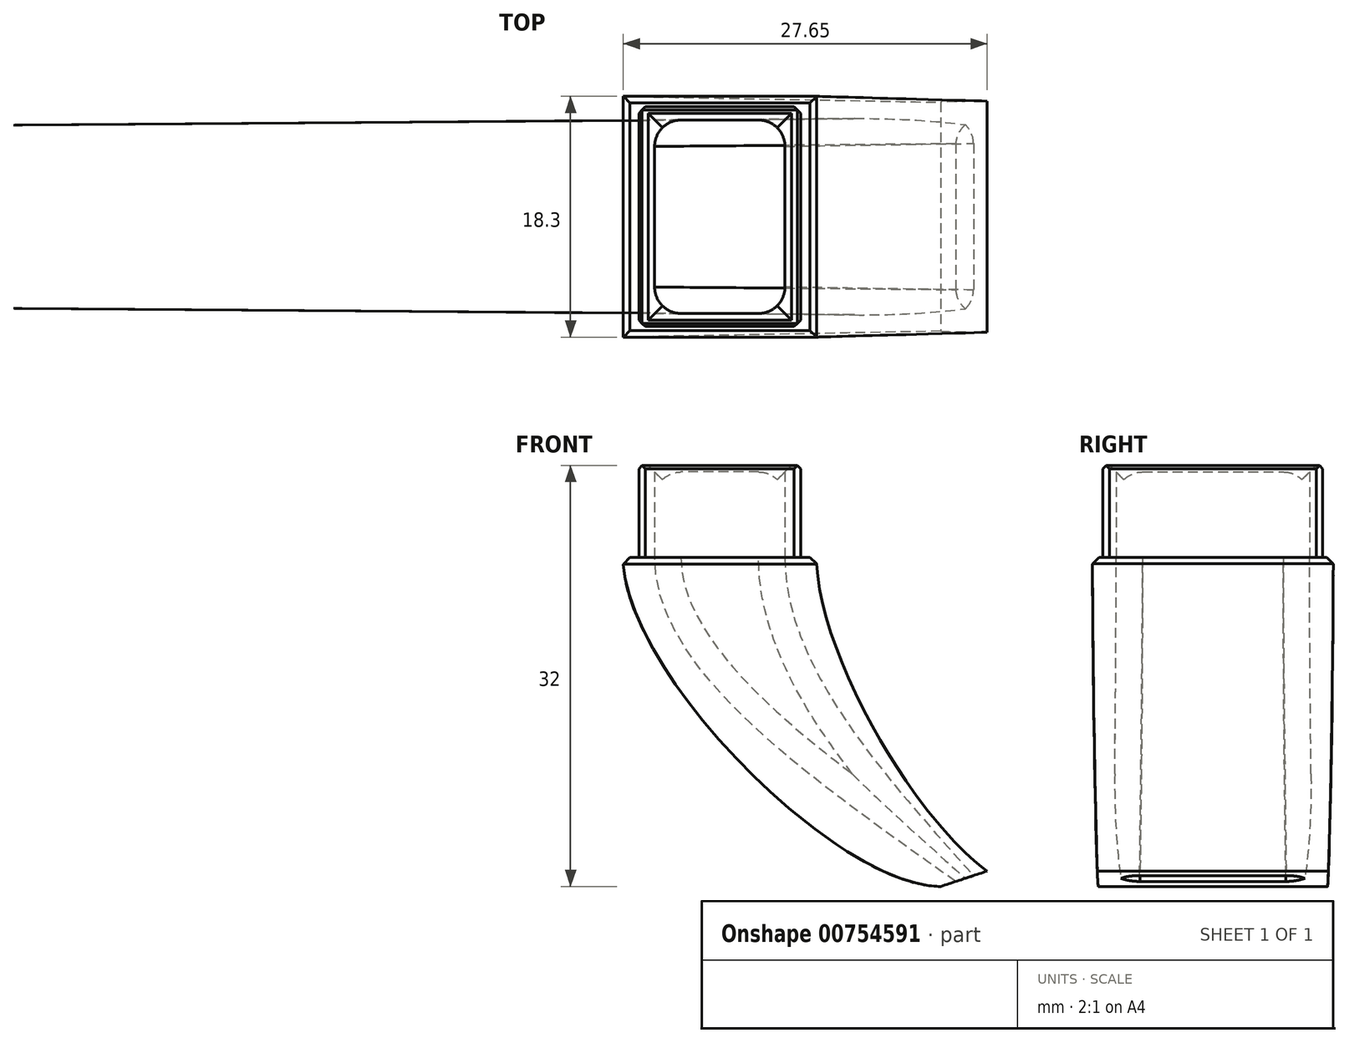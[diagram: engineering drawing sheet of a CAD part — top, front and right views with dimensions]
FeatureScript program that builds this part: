
annotation { "Feature Type Name" : "Feature", "Feature Type Description" : "" }
export const myFeature = defineFeature(function(context is Context, id is Id, definition is map)
    precondition{}
    {
        {
            var Q0;
            Q0=qCreatedBy(makeId("Top.planeOp"),FACE);
            var sketch = newSketch(context, id + "F0", { "sketchPlane" : qUnion([Q0])});
            skLineSegment(sketch, "E0.bottom", {"start": v(4.95, 7.35) * mm, "end": v(-4.95, 7.35) * mm});
            skLineSegment(sketch, "E0.top", {"start": v(4.95, -7.35) * mm, "end": v(-4.95, -7.35) * mm});
            skLineSegment(sketch, "E0.left", {"start": v(4.95, 7.35) * mm, "end": v(4.95, -7.35) * mm});
            skLineSegment(sketch, "E0.right", {"start": v(-4.95, 7.35) * mm, "end": v(-4.95, -7.35) * mm});
            skPoint(sketch, "E0.middle", {"position": v(0, 0) * mm});
            skLineSegment(sketch, "E1.bottom", {"start": v(6.15, 8.35) * mm, "end": v(-6.15, 8.35) * mm});
            skLineSegment(sketch, "E1.top", {"start": v(6.15, -8.35) * mm, "end": v(-6.15, -8.35) * mm});
            skLineSegment(sketch, "E1.left", {"start": v(6.15, 8.35) * mm, "end": v(6.15, -8.35) * mm});
            skLineSegment(sketch, "E1.right", {"start": v(-6.15, 8.35) * mm, "end": v(-6.15, -8.35) * mm});
            skSolve(sketch);
        }
        {
            var Q0;
            Q0 = qSketchRegion(id + "F0", true);
            extrude(context, id + "F1", {"entities" : qUnion([Q0]), "depth" : 7 * mm, "offsetDistance" : 25 * mm});
        }
        {
            var Q0;
            Q0=qCreatedBy(makeId("Top.planeOp"),FACE);
            var sketch = newSketch(context, id + "F2", { "sketchPlane" : qUnion([Q0])});
            skLineSegment(sketch, "E2.bottom", {"start": v(7.35, 9.15) * mm, "end": v(-7.35, 9.15) * mm});
            skLineSegment(sketch, "E2.top", {"start": v(7.35, -9.15) * mm, "end": v(-7.35, -9.15) * mm});
            skLineSegment(sketch, "E2.left", {"start": v(7.35, 9.15) * mm, "end": v(7.35, -9.15) * mm});
            skLineSegment(sketch, "E2.right", {"start": v(-7.35, 9.15) * mm, "end": v(-7.35, -9.15) * mm});
            skPoint(sketch, "E2.middle", {"position": v(0, 0) * mm});
            skSolve(sketch);
        }
        {
            var Q0;
            Q0=qCreatedBy(makeId("Top.planeOp"),FACE);
            cPlane(context, id + "F3", {"entities" : qUnion([Q0]), "cplaneType" : CPlaneType.OFFSET, "offset" : 25 * mm, "oppositeDirection" : true, "width" : 150 * mm, "height" : 150 * mm});
        }
        {
            var Q0;
            Q0=qCreatedBy(id+"F3.planeOp",FACE);
            var sketch = newSketch(context, id + "F4", { "sketchPlane" : qUnion([Q0])});
            skPoint(sketch, "E3.middle", {"position": v(20, 0) * mm});
            skLineSegment(sketch, "E4.bottom", {"start": v(23.2, 8.7) * mm, "end": v(16.8, 8.7) * mm});
            skLineSegment(sketch, "E4.top", {"start": v(23.2, -8.7) * mm, "end": v(16.8, -8.7) * mm});
            skLineSegment(sketch, "E4.left", {"start": v(23.2, 8.7) * mm, "end": v(23.2, -8.7) * mm});
            skLineSegment(sketch, "E4.right", {"start": v(16.8, 8.7) * mm, "end": v(16.8, -8.7) * mm});
            skSolve(sketch);
        }
        {
            var Q1;
            Q1 = qSketchRegion(id + "F2", true);
            var Q2;
            Q2 = qSketchRegion(id + "F4", true);
            loft(context, id + "F5", {"operationType" : NewBodyOperationType.ADD, "startCondition" : LoftEndDerivativeType.NORMAL_TO_PROFILE, "startMagnitude" : 1, "endCondition" : LoftEndDerivativeType.TANGENT_TO_PROFILE, "endMagnitude" : 1, "sheetProfilesArray" : [{ "sheetProfileEntities" : qUnion([Q1]) }, { "sheetProfileEntities" : qUnion([Q2]) }]});
        }
        {
            var Q0;
            Q0=qCreatedBy(makeId("Front.planeOp"),FACE);
            var sketch = newSketch(context, id + "F6", { "sketchPlane" : qUnion([Q0])});
            skLineSegment(sketch, "E5", {"start": v(16.8, -25) * mm, "end": v(20.4, -23.8) * mm});
            skLineSegment(sketch, "E6", {"start": v(20.4, -23.8) * mm, "end": v(25.23, -23.8) * mm});
            skLineSegment(sketch, "E7", {"start": v(25.23, -23.8) * mm, "end": v(25.23, -25) * mm});
            skLineSegment(sketch, "E8", {"start": v(25.23, -25) * mm, "end": v(16.8, -25) * mm});
            skSolve(sketch);
        }
        {
            var Q0;
            Q0 = qSketchRegion(id + "F6", true);
            extrude(context, id + "F7", {"entities" : qUnion([Q0]), "operationType" : NewBodyOperationType.REMOVE, "endBound" : BoundingType.SYMMETRIC, "oppositeDirection" : true, "depth" : 25 * mm, "offsetDistance" : 25 * mm});
        }
        {
            var Q0;
            Q0=makeQuery(id+"F7.boolean.opBoolean","COPY",FACE,{"derivedFrom":makeQuery(id+"F7.opExtrude","SWEPT_FACE",FACE,{"disambiguationData":[OSD([sQuery(id+"F6.wireOp",EDGE,"E5")])]})});
            var sketch = newSketch(context, id + "F8", { "sketchPlane" : qUnion([Q0])});
            skLineSegment(sketch, "E9.bottom", {"start": v(9.23, -7.56) * mm, "end": v(10.65, -7.56) * mm});
            skLineSegment(sketch, "E9.top", {"start": v(9.23, 7.56) * mm, "end": v(10.65, 7.56) * mm});
            skLineSegment(sketch, "E9.left", {"start": v(9.23, -7.56) * mm, "end": v(9.23, 7.56) * mm});
            skLineSegment(sketch, "E9.right", {"start": v(10.65, -7.56) * mm, "end": v(10.65, 7.56) * mm});
            skPoint(sketch, "E9.middle", {"position": v(9.94, 0) * mm});
            skSolve(sketch);
        }
        {
            var Q1;
            Q1=makeQuery(id+"F5.boolean.opBoolean","SPLIT",FACE,{"disambiguationData":[TD([makeQuery(id+"F1.opExtrude","SWEPT_FACE",FACE,{"disambiguationData":[OSD([sQuery(id+"F0.wireOp",EDGE,"E0.bottom")])]})])],"derivedFrom":makeQuery(id+"F5.opLoft","CAP_FACE",FACE,{"disambiguationData":[OSD([makeQuery(id+"F2.imprint","IMPRINT",FACE,{"disambiguationData":[TD([[makeQuery(id+"F2.imprint","IMPRINT",EDGE,{"derivedFrom":sQuery(id+"F2.wireOp",EDGE,"E2.bottom")}),1.0]])]})])],"isStart":true})});
            var Q2;
            Q2 = qSketchRegion(id + "F8", true);
            loft(context, id + "F9", {"operationType" : NewBodyOperationType.REMOVE, "startCondition" : LoftEndDerivativeType.NORMAL_TO_PROFILE, "startMagnitude" : 1, "sheetProfilesArray" : [{ "sheetProfileEntities" : qUnion([Q1]) }, { "sheetProfileEntities" : qUnion([Q2]) }]});
        }
        {
            var Q0;
            Q0=makeQuery(id+"F1.opExtrude","CAP_EDGE",EDGE,{"disambiguationData":[OSD([sQuery(id+"F0.wireOp",EDGE,"E0.right")])],"isStart":false});
            var Q1;
            Q1=makeQuery(id+"F1.opExtrude","CAP_EDGE",EDGE,{"disambiguationData":[OSD([sQuery(id+"F0.wireOp",EDGE,"E0.bottom")])],"isStart":false});
            var Q2;
            Q2=makeQuery(id+"F1.opExtrude","CAP_EDGE",EDGE,{"disambiguationData":[OSD([sQuery(id+"F0.wireOp",EDGE,"E0.left")])],"isStart":false});
            var Q3;
            Q3=makeQuery(id+"F1.opExtrude","CAP_EDGE",EDGE,{"disambiguationData":[OSD([sQuery(id+"F0.wireOp",EDGE,"E0.top")])],"isStart":false});
            var Q4;
            Q4=makeQuery(id+"F1.opExtrude","SWEPT_EDGE",EDGE,{"disambiguationData":[OSD([sQuery(id+"F0.wireOp",EDGE,"E1.bottom"),sQuery(id+"F0.wireOp",EDGE,"E1.left")])]});
            var Q5;
            Q5=makeQuery(id+"F1.opExtrude","SWEPT_EDGE",EDGE,{"disambiguationData":[OSD([sQuery(id+"F0.wireOp",EDGE,"E1.top"),sQuery(id+"F0.wireOp",EDGE,"E1.left")])]});
            var Q6;
            Q6=makeQuery(id+"F1.opExtrude","SWEPT_EDGE",EDGE,{"disambiguationData":[OSD([sQuery(id+"F0.wireOp",EDGE,"E1.top"),sQuery(id+"F0.wireOp",EDGE,"E1.right")])]});
            var Q7;
            Q7=makeQuery(id+"F1.opExtrude","SWEPT_EDGE",EDGE,{"disambiguationData":[OSD([sQuery(id+"F0.wireOp",EDGE,"E1.bottom"),sQuery(id+"F0.wireOp",EDGE,"E1.right")])]});
            chamfer(context, id + "F10", {"entities" : qUnion([Q0, Q1, Q2, Q3, Q4, Q5, Q6, Q7]), "width" : .5 * mm, "tangentPropagation" : true});
        }
        {
            var Q0;
            Q0=makeQuery(id+"F9.boolean.opBoolean","COPY",EDGE,{"derivedFrom":makeQuery(id+"F9.opLoft","SWEPT_EDGE",EDGE,{"disambiguationData":[OSD([sQuery(id+"F0.wireOp",EDGE,"E0.bottom"),sQuery(id+"F0.wireOp",EDGE,"E0.left"),sQuery(id+"F8.wireOp",EDGE,"E9.bottom"),sQuery(id+"F8.wireOp",EDGE,"E9.right")])]})});
            var Q1;
            Q1=makeQuery(id+"F9.boolean.opBoolean","COPY",EDGE,{"derivedFrom":makeQuery(id+"F9.opLoft","SWEPT_EDGE",EDGE,{"disambiguationData":[OSD([sQuery(id+"F0.wireOp",EDGE,"E0.bottom"),sQuery(id+"F0.wireOp",EDGE,"E0.right"),sQuery(id+"F8.wireOp",EDGE,"E9.bottom"),sQuery(id+"F8.wireOp",EDGE,"E9.left")])]})});
            var Q2;
            Q2=makeQuery(id+"F9.boolean.opBoolean","COPY",EDGE,{"derivedFrom":makeQuery(id+"F9.opLoft","SWEPT_EDGE",EDGE,{"disambiguationData":[OSD([sQuery(id+"F0.wireOp",EDGE,"E0.top"),sQuery(id+"F0.wireOp",EDGE,"E0.right"),sQuery(id+"F8.wireOp",EDGE,"E9.top"),sQuery(id+"F8.wireOp",EDGE,"E9.left")])]})});
            var Q3;
            Q3=makeQuery(id+"F9.boolean.opBoolean","COPY",EDGE,{"derivedFrom":makeQuery(id+"F9.opLoft","SWEPT_EDGE",EDGE,{"disambiguationData":[OSD([sQuery(id+"F0.wireOp",EDGE,"E0.top"),sQuery(id+"F0.wireOp",EDGE,"E0.left"),sQuery(id+"F8.wireOp",EDGE,"E9.top"),sQuery(id+"F8.wireOp",EDGE,"E9.right")])]})});
            fillet(context, id + "F11", {"entities" : qUnion([Q0, Q1, Q2, Q3]), "radius" : 2 * mm, "tangentPropagation" : true, "allowEdgeOverflow" : false});
        }
        {
            var Q0;
            Q0=makeQuery(id+"F5.opLoft","MID_CAP_EDGE",EDGE,{"disambiguationData":[OSD([sQuery(id+"F2.wireOp",EDGE,"E2.bottom"),sQuery(id+"F2.wireOp",EDGE,"E2.top"),sQuery(id+"F2.wireOp",EDGE,"E2.right")])],"capPos":0.0});
            var Q1;
            Q1=makeQuery(id+"F5.opLoft","MID_CAP_EDGE",EDGE,{"disambiguationData":[OSD([sQuery(id+"F2.wireOp",EDGE,"E2.top"),sQuery(id+"F2.wireOp",EDGE,"E2.left"),sQuery(id+"F2.wireOp",EDGE,"E2.right")])],"capPos":0.0});
            var Q2;
            Q2=makeQuery(id+"F5.opLoft","MID_CAP_EDGE",EDGE,{"disambiguationData":[OSD([sQuery(id+"F2.wireOp",EDGE,"E2.bottom"),sQuery(id+"F2.wireOp",EDGE,"E2.top"),sQuery(id+"F2.wireOp",EDGE,"E2.left")])],"capPos":0.0});
            var Q3;
            Q3=makeQuery(id+"F5.opLoft","MID_CAP_EDGE",EDGE,{"disambiguationData":[OSD([sQuery(id+"F2.wireOp",EDGE,"E2.bottom"),sQuery(id+"F2.wireOp",EDGE,"E2.left"),sQuery(id+"F2.wireOp",EDGE,"E2.right")])],"capPos":0.0});
            chamfer(context, id + "F12", {"entities" : qUnion([Q0, Q1, Q2, Q3]), "width" : .5 * mm, "tangentPropagation" : true});
        }
        {
            var Q0;
            Q0=makeQuery(id+"F1.opExtrude","CAP_EDGE",EDGE,{"disambiguationData":[OSD([sQuery(id+"F0.wireOp",EDGE,"E1.left")])],"isStart":false});
            var Q1;
            Q1=makeQuery(id+"F1.opExtrude","CAP_EDGE",EDGE,{"disambiguationData":[OSD([sQuery(id+"F0.wireOp",EDGE,"E1.top")])],"isStart":false});
            var Q2;
            Q2=makeQuery(id+"F1.opExtrude","CAP_EDGE",EDGE,{"disambiguationData":[OSD([sQuery(id+"F0.wireOp",EDGE,"E1.right")])],"isStart":false});
            var Q3;
            Q3=makeQuery(id+"F1.opExtrude","CAP_EDGE",EDGE,{"disambiguationData":[OSD([sQuery(id+"F0.wireOp",EDGE,"E1.bottom")])],"isStart":false});
            chamfer(context, id + "F13", {"entities" : qUnion([Q0, Q1, Q2, Q3]), "width" : .25 * mm, "tangentPropagation" : true});
        }
    });
